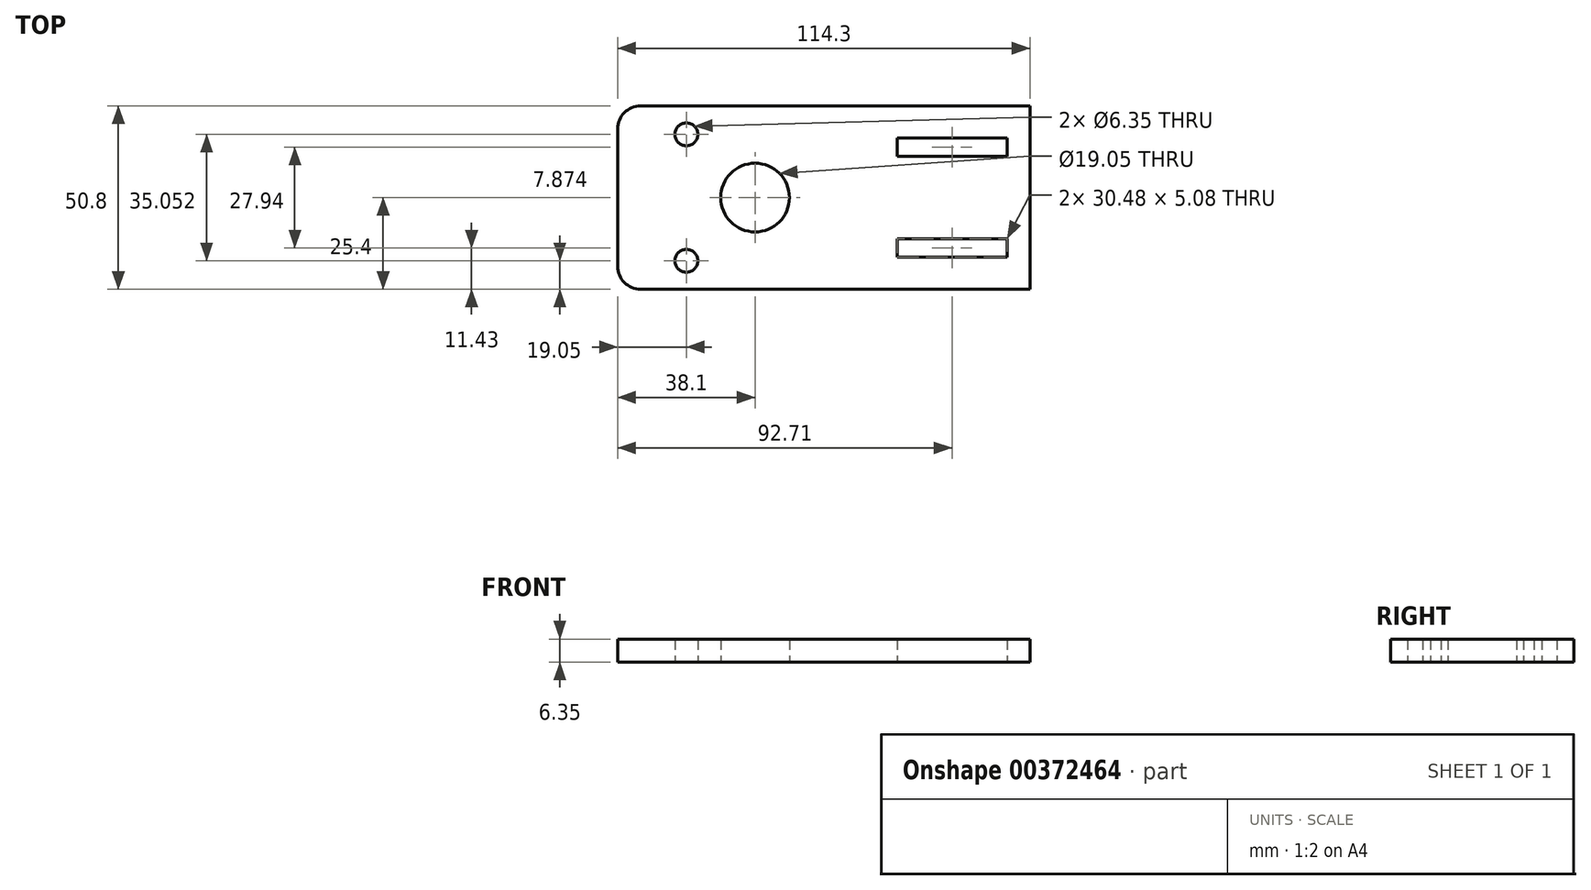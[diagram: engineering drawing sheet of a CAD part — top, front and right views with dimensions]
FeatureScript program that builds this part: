
annotation { "Feature Type Name" : "Feature", "Feature Type Description" : "" }
export const myFeature = defineFeature(function(context is Context, id is Id, definition is map)
    precondition{}
    {
        {
            var Q0;
            Q0=qCreatedBy(makeId("Top.planeOp"),FACE);
            var sketch = newSketch(context, id + "F0", { "sketchPlane" : qUnion([Q0])});
            skLineSegment(sketch, "E0.bottom", {"start": v(38.1, 25.4) * mm, "end": v(-38.1, 25.4) * mm});
            skLineSegment(sketch, "E0.top", {"start": v(38.1, -25.4) * mm, "end": v(-38.1, -25.4) * mm});
            skLineSegment(sketch, "E0.left", {"start": v(38.1, 25.4) * mm, "end": v(38.1, -25.4) * mm});
            skLineSegment(sketch, "E0.right", {"start": v(-38.1, 25.4) * mm, "end": v(-38.1, -25.4) * mm});
            skPoint(sketch, "E0.middle", {"position": v(0, 0) * mm});
            skCircle(sketch, "E1", {"center": v(-38.1, 0) * mm, "radius": 9.53 * mm});
            skLineSegment(sketch, "E2.bottom", {"start": v(31.75, 11.43) * mm, "end": v(1.27, 11.43) * mm});
            skLineSegment(sketch, "E2.top", {"start": v(31.75, 16.5) * mm, "end": v(1.27, 16.5) * mm});
            skLineSegment(sketch, "E2.left", {"start": v(31.75, 11.43) * mm, "end": v(31.75, 16.5) * mm});
            skLineSegment(sketch, "E2.right", {"start": v(1.27, 11.43) * mm, "end": v(1.27, 16.5) * mm});
            skPoint(sketch, "E2.middle", {"position": v(16.51, 13.97) * mm});
            skLineSegment(sketch, "E3.bottom", {"start": v(31.75, -16.51) * mm, "end": v(1.27, -16.51) * mm});
            skLineSegment(sketch, "E3.top", {"start": v(31.75, -11.43) * mm, "end": v(1.27, -11.43) * mm});
            skLineSegment(sketch, "E3.left", {"start": v(31.75, -16.51) * mm, "end": v(31.75, -11.43) * mm});
            skLineSegment(sketch, "E3.right", {"start": v(1.27, -16.51) * mm, "end": v(1.27, -11.43) * mm});
            skPoint(sketch, "E3.middle", {"position": v(16.51, -13.97) * mm});
            skLineSegment(sketch, "E4.bottom", {"start": v(-38.1, 25.4) * mm, "end": v(-69.85, 25.4) * mm});
            skLineSegment(sketch, "E4.top", {"start": v(-38.1, -25.4) * mm, "end": v(-69.85, -25.4) * mm});
            skLineSegment(sketch, "E4.right", {"start": v(-76.2, 19.05) * mm, "end": v(-76.2, -19.05) * mm});
            skArc(sketch, "E5.filletArc", {"start": v(-69.85, 25.4) * mm, "mid": v(-74.34, 23.54) * mm, "end": v(-76.2, 19.05) * mm});
            skArc(sketch, "E6.filletArc", {"start": v(-76.2, -19.05) * mm, "mid": v(-74.34, -23.54) * mm, "end": v(-69.85, -25.4) * mm});
            skPoint(sketch, "E7", {"position": v(-57.15, 25.4) * mm});
            skCircle(sketch, "E8", {"center": v(-57.15, 17.53) * mm, "radius": 3.18 * mm});
            skCircle(sketch, "E9", {"center": v(-57.15, -17.53) * mm, "radius": 3.18 * mm});
            skSolve(sketch);
        }
        {
            var Q0;
            Q0 = qSketchRegion(id + "F0", true);
            extrude(context, id + "F1", {"entities" : qUnion([Q0]), "depth" : 6.35 * mm});
        }
        {
            var Q0;
            Q0=makeQuery(id+"F1.opExtrude","CAP_FACE",FACE,{"disambiguationData":[OSD([sQuery(id+"F0.wireOp",EDGE,"E0.bottom"),sQuery(id+"F0.wireOp",EDGE,"E0.top"),sQuery(id+"F0.wireOp",EDGE,"E0.left"),sQuery(id+"F0.wireOp",EDGE,"30ab1acb-bd41-426d-b47f-3a6df886cf8d"),sQuery(id+"F0.wireOp",EDGE,"E1"),sQuery(id+"F0.wireOp",EDGE,"E2.bottom"),sQuery(id+"F0.wireOp",EDGE,"E2.top"),sQuery(id+"F0.wireOp",EDGE,"E2.left"),sQuery(id+"F0.wireOp",EDGE,"E2.right"),sQuery(id+"F0.wireOp",EDGE,"E3.bottom"),sQuery(id+"F0.wireOp",EDGE,"E3.top"),sQuery(id+"F0.wireOp",EDGE,"E3.left"),sQuery(id+"F0.wireOp",EDGE,"E3.right")])],"isStart":false});
            extrude(context, id + "F2", {"entities" : qUnion([Q0]), "operationType" : NewBodyOperationType.ADD, "oppositeDirection" : true, "depth" : 6.35 * mm});
        }
    });
